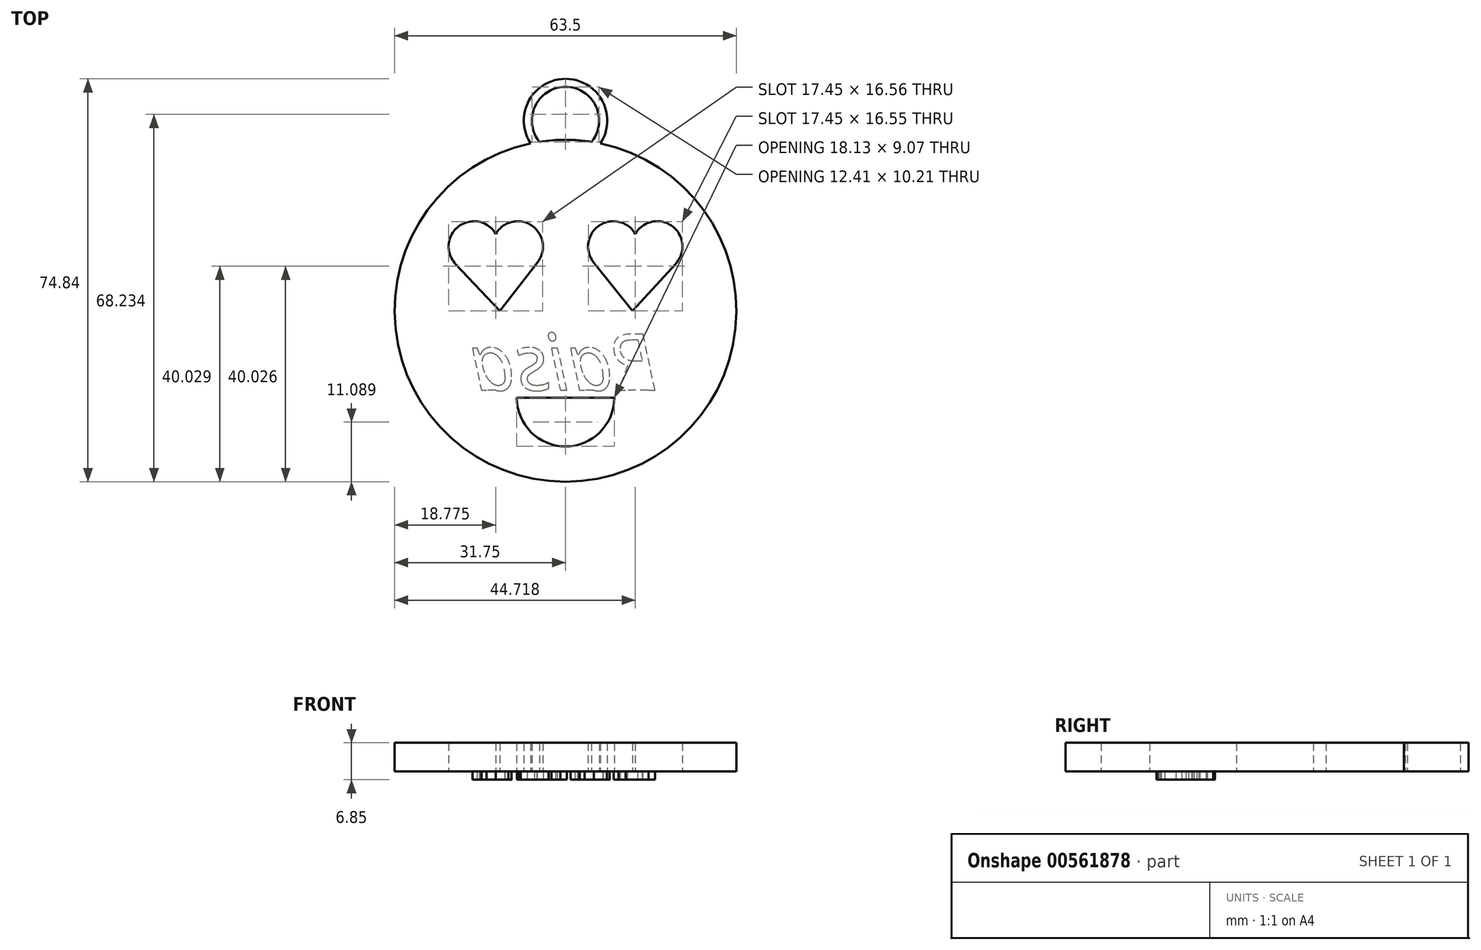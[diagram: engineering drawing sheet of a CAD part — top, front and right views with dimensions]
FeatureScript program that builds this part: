
annotation { "Feature Type Name" : "Feature", "Feature Type Description" : "" }
export const myFeature = defineFeature(function(context is Context, id is Id, definition is map)
    precondition{}
    {
        {
            var Q0;
            Q0=qCreatedBy(makeId("Top.planeOp"),FACE);
            var sketch = newSketch(context, id + "F0", { "sketchPlane" : qUnion([Q0])});
            skCircle(sketch, "E0", {"center": v(0, 0) * mm, "radius": 31.75 * mm});
            skPoint(sketch, "E1", {"position": v(-12.32, 11.94) * mm});
            skPoint(sketch, "E2", {"position": v(8.9, 11.94) * mm});
            skCircle(sketch, "E3", {"center": v(-17.02, 11.94) * mm, "radius": 4.7 * mm});
            skCircle(sketch, "E4", {"center": v(-8.9, 11.94) * mm, "radius": 4.7 * mm});
            skCircle(sketch, "E5", {"center": v(17.02, 11.94) * mm, "radius": 4.7 * mm});
            skCircle(sketch, "E6", {"center": v(8.9, 11.94) * mm, "radius": 4.7 * mm});
            skPoint(sketch, "E7", {"position": v(-12.2, 0) * mm});
            skPoint(sketch, "E8", {"position": v(12.47, 0) * mm});
            skLineSegment(sketch, "E9", {"start": v(12.47, 0) * mm, "end": v(20.49, 8.77) * mm});
            skLineSegment(sketch, "E10", {"start": v(12.47, 0) * mm, "end": v(5.23, 9) * mm});
            skLineSegment(sketch, "E11", {"start": v(-12.2, 0) * mm, "end": v(-5.18, 9.06) * mm});
            skLineSegment(sketch, "E12", {"start": v(-12.2, 0) * mm, "end": v(-20.43, 8.7) * mm});
            skCircle(sketch, "E13", {"center": v(0, -16.13) * mm, "radius": 9.07 * mm});
            skLineSegment(sketch, "E14", {"start": v(-9.07, -16.13) * mm, "end": v(9.07, -16.13) * mm});
            skSolve(sketch);
        }
        {
            var Q0;
            Q0=makeQuery(id+"F0.imprint","IMPRINT",FACE,{"disambiguationData":[TD([[makeQuery(id+"F0.imprint","IMPRINT",EDGE,{"derivedFrom":sQuery(id+"F0.wireOp",EDGE,"E0")}),1.0]])]});
            var Q1;
            {var subQ4=sQuery(id+"F0.wireOp",EDGE,"E11");Q1=makeQuery(id+"F0.imprint","IMPRINT",FACE,{"disambiguationData":[TD([[makeQuery(id+"F0.imprint","IMPRINT",EDGE,{"derivedFrom":subQ4}),1.0]])]});}
            var Q2;
            {var subQ0=sQuery(id+"F0.wireOp",EDGE,"E3");var subQ1=makeQuery(id+"F0.imprint","INTERSECT",VERTEX,{"derivedFrom":[subQ0,sQuery(id+"F0.wireOp",EDGE,"E12")]});Q2=makeQuery(id+"F0.imprint","IMPRINT",FACE,{"disambiguationData":[TD([[makeQuery(id+"F0.imprint","IMPRINT",EDGE,{"disambiguationData":[TD([[subQ1,1.0]])],"derivedFrom":subQ0}),1.0]])]});}
            var Q3;
            {var subQ0=sQuery(id+"F0.wireOp",EDGE,"E6");var subQ1=sQuery(id+"F0.wireOp",EDGE,"E5");var subQ2=makeQuery(id+"F0.imprint","INTERSECT",VERTEX,{"disambiguationData":[OD(0.0)],"derivedFrom":[subQ1,subQ0]});Q3=makeQuery(id+"F0.imprint","IMPRINT",FACE,{"disambiguationData":[TD([[makeQuery(id+"F0.imprint","IMPRINT",EDGE,{"disambiguationData":[TD([[subQ2,1.0]])],"derivedFrom":subQ1}),-1.0]])]});}
            var Q4;
            {var subQ0=sQuery(id+"F0.wireOp",EDGE,"E9");Q4=makeQuery(id+"F0.imprint","IMPRINT",FACE,{"disambiguationData":[TD([[makeQuery(id+"F0.imprint","IMPRINT",EDGE,{"derivedFrom":subQ0}),1.0]])]});}
            var Q5;
            {var subQ0=sQuery(id+"F0.wireOp",EDGE,"E4");var subQ1=sQuery(id+"F0.wireOp",EDGE,"E3");var subQ2=makeQuery(id+"F0.imprint","INTERSECT",VERTEX,{"disambiguationData":[OD(0.0)],"derivedFrom":[subQ1,subQ0]});Q5=makeQuery(id+"F0.imprint","IMPRINT",FACE,{"disambiguationData":[TD([[makeQuery(id+"F0.imprint","IMPRINT",EDGE,{"disambiguationData":[TD([[subQ2,1.0]])],"derivedFrom":subQ1}),-1.0]])]});}
            var Q6;
            {var subQ0=sQuery(id+"F0.wireOp",EDGE,"E4");var subQ1=sQuery(id+"F0.wireOp",EDGE,"E3");var subQ2=makeQuery(id+"F0.imprint","INTERSECT",VERTEX,{"disambiguationData":[OD(0.0)],"derivedFrom":[subQ1,subQ0]});Q6=makeQuery(id+"F0.imprint","IMPRINT",FACE,{"disambiguationData":[TD([[makeQuery(id+"F0.imprint","IMPRINT",EDGE,{"disambiguationData":[TD([[subQ2,1.0]])],"derivedFrom":subQ1}),1.0]])]});}
            var Q7;
            {var subQ0=sQuery(id+"F0.wireOp",EDGE,"E5");var subQ1=makeQuery(id+"F0.imprint","INTERSECT",VERTEX,{"derivedFrom":[subQ0,sQuery(id+"F0.wireOp",EDGE,"E9")]});Q7=makeQuery(id+"F0.imprint","IMPRINT",FACE,{"disambiguationData":[TD([[makeQuery(id+"F0.imprint","IMPRINT",EDGE,{"disambiguationData":[TD([[subQ1,1.0]])],"derivedFrom":subQ0}),1.0]])]});}
            var Q8;
            {var subQ0=sQuery(id+"F0.wireOp",EDGE,"E6");var subQ1=sQuery(id+"F0.wireOp",EDGE,"E5");var subQ2=makeQuery(id+"F0.imprint","INTERSECT",VERTEX,{"disambiguationData":[OD(0.0)],"derivedFrom":[subQ1,subQ0]});Q8=makeQuery(id+"F0.imprint","IMPRINT",FACE,{"disambiguationData":[TD([[makeQuery(id+"F0.imprint","IMPRINT",EDGE,{"disambiguationData":[TD([[subQ2,1.0]])],"derivedFrom":subQ1}),1.0]])]});}
            var Q9;
            {var subQ0=sQuery(id+"F0.wireOp",EDGE,"E14");Q9=makeQuery(id+"F0.imprint","IMPRINT",FACE,{"disambiguationData":[TD([[makeQuery(id+"F0.imprint","IMPRINT",EDGE,{"derivedFrom":subQ0}),1.0]])]});}
            var Q10;
            {var subQ0=sQuery(id+"F0.wireOp",EDGE,"E14");Q10=makeQuery(id+"F0.imprint","IMPRINT",FACE,{"disambiguationData":[TD([[makeQuery(id+"F0.imprint","IMPRINT",EDGE,{"derivedFrom":subQ0}),-1.0]])]});}
            extrude(context, id + "F1", {"entities" : qUnion([Q0, Q1, Q2, Q3, Q4, Q5, Q6, Q7, Q8, Q9, Q10]), "depth" : 5.33 * mm, "offsetDistance" : 25.4 * mm});
        }
        {
            var Q0;
            {var subQ0=sQuery(id+"F0.wireOp",EDGE,"E5");var subQ1=makeQuery(id+"F0.imprint","INTERSECT",VERTEX,{"derivedFrom":[subQ0,sQuery(id+"F0.wireOp",EDGE,"E9")]});Q0=makeQuery(id+"F0.imprint","IMPRINT",FACE,{"disambiguationData":[TD([[makeQuery(id+"F0.imprint","IMPRINT",EDGE,{"disambiguationData":[TD([[subQ1,1.0]])],"derivedFrom":subQ0}),1.0]])]});}
            var Q1;
            {var subQ0=sQuery(id+"F0.wireOp",EDGE,"E9");Q1=makeQuery(id+"F0.imprint","IMPRINT",FACE,{"disambiguationData":[TD([[makeQuery(id+"F0.imprint","IMPRINT",EDGE,{"derivedFrom":subQ0}),1.0]])]});}
            var Q2;
            {var subQ0=sQuery(id+"F0.wireOp",EDGE,"E4");var subQ1=sQuery(id+"F0.wireOp",EDGE,"E3");var subQ2=makeQuery(id+"F0.imprint","INTERSECT",VERTEX,{"disambiguationData":[OD(0.0)],"derivedFrom":[subQ1,subQ0]});Q2=makeQuery(id+"F0.imprint","IMPRINT",FACE,{"disambiguationData":[TD([[makeQuery(id+"F0.imprint","IMPRINT",EDGE,{"disambiguationData":[TD([[subQ2,1.0]])],"derivedFrom":subQ1}),-1.0]])]});}
            var Q3;
            {var subQ0=sQuery(id+"F0.wireOp",EDGE,"E3");var subQ1=makeQuery(id+"F0.imprint","INTERSECT",VERTEX,{"derivedFrom":[subQ0,sQuery(id+"F0.wireOp",EDGE,"E12")]});Q3=makeQuery(id+"F0.imprint","IMPRINT",FACE,{"disambiguationData":[TD([[makeQuery(id+"F0.imprint","IMPRINT",EDGE,{"disambiguationData":[TD([[subQ1,1.0]])],"derivedFrom":subQ0}),1.0]])]});}
            var Q4;
            {var subQ4=sQuery(id+"F0.wireOp",EDGE,"E11");Q4=makeQuery(id+"F0.imprint","IMPRINT",FACE,{"disambiguationData":[TD([[makeQuery(id+"F0.imprint","IMPRINT",EDGE,{"derivedFrom":subQ4}),1.0]])]});}
            var Q5;
            {var subQ0=sQuery(id+"F0.wireOp",EDGE,"E14");Q5=makeQuery(id+"F0.imprint","IMPRINT",FACE,{"disambiguationData":[TD([[makeQuery(id+"F0.imprint","IMPRINT",EDGE,{"derivedFrom":subQ0}),-1.0]])]});}
            var Q6;
            {var subQ0=sQuery(id+"F0.wireOp",EDGE,"E6");var subQ1=sQuery(id+"F0.wireOp",EDGE,"E5");var subQ2=makeQuery(id+"F0.imprint","INTERSECT",VERTEX,{"disambiguationData":[OD(0.0)],"derivedFrom":[subQ1,subQ0]});Q6=makeQuery(id+"F0.imprint","IMPRINT",FACE,{"disambiguationData":[TD([[makeQuery(id+"F0.imprint","IMPRINT",EDGE,{"disambiguationData":[TD([[subQ2,1.0]])],"derivedFrom":subQ1}),-1.0]])]});}
            var Q7;
            {var subQ0=sQuery(id+"F0.wireOp",EDGE,"E6");var subQ1=sQuery(id+"F0.wireOp",EDGE,"E5");var subQ2=makeQuery(id+"F0.imprint","INTERSECT",VERTEX,{"disambiguationData":[OD(0.0)],"derivedFrom":[subQ1,subQ0]});Q7=makeQuery(id+"F0.imprint","IMPRINT",FACE,{"disambiguationData":[TD([[makeQuery(id+"F0.imprint","IMPRINT",EDGE,{"disambiguationData":[TD([[subQ2,1.0]])],"derivedFrom":subQ1}),1.0]])]});}
            var Q8;
            {var subQ0=sQuery(id+"F0.wireOp",EDGE,"E4");var subQ1=sQuery(id+"F0.wireOp",EDGE,"E3");var subQ2=makeQuery(id+"F0.imprint","INTERSECT",VERTEX,{"disambiguationData":[OD(0.0)],"derivedFrom":[subQ1,subQ0]});Q8=makeQuery(id+"F0.imprint","IMPRINT",FACE,{"disambiguationData":[TD([[makeQuery(id+"F0.imprint","IMPRINT",EDGE,{"disambiguationData":[TD([[subQ2,1.0]])],"derivedFrom":subQ1}),1.0]])]});}
            extrude(context, id + "F2", {"entities" : qUnion([Q0, Q1, Q2, Q3, Q4, Q5, Q6, Q7, Q8]), "operationType" : NewBodyOperationType.REMOVE, "depth" : 9.7 * mm, "offsetDistance" : 25.4 * mm});
        }
        {
            var Q0;
            Q0=makeQuery(id+"F1.opExtrude","CAP_FACE",FACE,{"disambiguationData":[OSD([sQuery(id+"F0.wireOp",EDGE,"E0")])],"isStart":true});
            var sketch = newSketch(context, id + "F3", { "sketchPlane" : qUnion([Q0])});
            skCircle(sketch, "E15", {"center": v(0, -35.34) * mm, "radius": 6.25 * mm});
            skCircle(sketch, "E16", {"center": v(0, -35.34) * mm, "radius": 7.75 * mm});
            skSolve(sketch);
        }
        {
            var Q0;
            {var subQ0=sQuery(id+"F3.wireOp",EDGE,"E15");var subQ1=makeQuery(id+"F1.opExtrude","CAP_EDGE",EDGE,{"disambiguationData":[OSD([sQuery(id+"F0.wireOp",EDGE,"E0")])],"isStart":true});var subQ2=makeQuery(id+"F3.imprint","INTERSECT",VERTEX,{"disambiguationData":[OD(0.0)],"derivedFrom":[subQ1,subQ0]});Q0=makeQuery(id+"F3.imprint","IMPRINT",FACE,{"disambiguationData":[TD([[makeQuery(id+"F3.imprint","IMPRINT",EDGE,{"disambiguationData":[TD([[subQ2,-1.0]])],"derivedFrom":subQ0}),-1.0]])]});}
            extrude(context, id + "F4", {"entities" : qUnion([Q0]), "operationType" : NewBodyOperationType.ADD, "oppositeDirection" : true, "depth" : 5.33 * mm, "offsetDistance" : 25.4 * mm});
        }
        {
            var Q0;
            {var subQ0=sQuery(id+"F0.wireOp",EDGE,"E0");Q0=makeQuery(id+"F4.boolean.opBoolean","MERGE",FACE,{"derivedFrom":[makeQuery(id+"F1.opExtrude","CAP_FACE",FACE,{"disambiguationData":[OSD([subQ0])],"isStart":true}),makeQuery(id+"F4.opExtrude","CAP_FACE",FACE,{"disambiguationData":[OSD([subQ0,sQuery(id+"F3.wireOp",EDGE,"E15"),sQuery(id+"F3.wireOp",EDGE,"E16")])],"isStart":true})]});}
            var sketch = newSketch(context, id + "F5", { "sketchPlane" : qUnion([Q0])});
            skText(sketch, "E17", { "text": "Raisa", "fontName": "OpenSans-Italic.ttf"});
            skLineSegment(sketch, "E18", {"start": v(17.22, 14.75) * mm, "end": v(-18.27, 14.75) * mm});
            const initialGuessF5  = {"E17": [0.01722, 0.01475, -1, 0, 0.01052]};
            skSetInitialGuess(sketch, initialGuessF5);
            skSolve(sketch);
        }
        {
            var Q0;
            Q0 = qSketchRegion(id + "F5", true);
            extrude(context, id + "F6", {"entities" : qUnion([Q0]), "operationType" : NewBodyOperationType.ADD, "depth" : 1.52 * mm, "offsetDistance" : 25.4 * mm});
        }
    });
